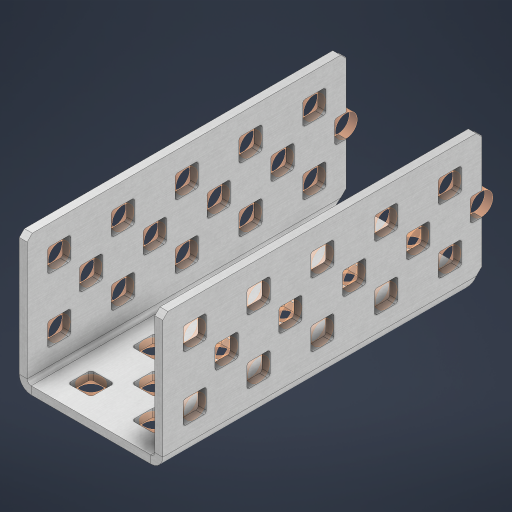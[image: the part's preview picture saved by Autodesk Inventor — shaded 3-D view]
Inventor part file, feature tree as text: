
AUTODESK INVENTOR PART (.ipt)
format: ipt  version: 2023 (Build 270158000, 158)  size: 959,488 bytes
history: native  units: in
note: dims shown in document units (in); Inventor stores cm internally (conversion verified against a paired STEP export)
features: other x66, extrude x58, sheet_metal_op x8, sketch x7, mirror x3, pattern_linear x2, chamfer x1
ambient origin geometry x8: Origin, YZ Plane, XZ Plane, XY Plane, X Axis, Y Axis, Z Axis, Center Point
bodies: Solid1 (feature_tree), Body (feature_tree)
feature tree (145):
  sheet_metal_op  "Flanges"
  sheet_metal_op  "Body Pattern"
  pattern_linear  "Center Pattern"  Spacing1=1.0in  [1 undecoded]
  other  "Arc Length"
  mirror  "Notch Mirror"
  pattern_linear  "Notch Pattern"  Spacing1=0.25in  [1 undecoded]
  other  "Diagonal Plane"
  mirror  "Flange 1"
  mirror  "Flange 2"
  chamfer  "End Chamfer"
  sketch  "Sketch1"  dims[d0=1.0in]
  other  "Plate1"
  sketch  "Sketch2"  dims[d1=2.5in]
  other  "Plate2"
  sheet_metal_op  "Bend1"
  sheet_metal_op  "Corner1"
  sketch  "Sketch8"  dims[d2=0.0625in]
  sketch  "Sketch9"  dims[d3=0.0625in]
  other  "Srf91"
  sheet_metal_op  "Body Pattern Sketch"
  other  "Srf92"
  sketch  "Sketch13"  dims[d4=0.0312in]
  sketch  "Sketch15"  dims[d5=0.125in]
  sketch  "Sketch16"  dims[d6=0.0625in d7=1.0in d8=90.0deg d9=0.0312in d10=0.25in d11=0.0625in d12=0.0625in d49=0.182in d50=0.02in d52=0.25in d53=0.0625in d54=0.0in d55=0.172in d56=1.0in d57=0.0in d60=1.9685in d62=0.5in d63=0.7874in d65=0.5in d85=0.1473in d86=0.1782in d88=0.04in d89=0.0625in d90=0.0in d91=0.04in d92=0.0491in d95=2.5in d96=0.04in d97=0.25in d98=45.0deg d99=0.25in d102=2.497in d106=0.182in d107=0.02in d108=0.5in d110=0.0625in d111=0.0in d112=0.172in d113=0.5in d114=0.0in d117=0.5in d118=0.5in d131=0.25in d132=0.25in]
  other  "Srf786"
  other  "Srf889"
  other  "Srf890"
  other  "Srf891"
  other  "Srf892"
  other  "Srf1315"
  other  "Srf1316"
  other  "Srf1317"
  other  "Srf1325"
  other  "Srf1326"
  other  "Srf1327"
  other  "Srf1328"
  other  "Srf1374"
  other  "Srf1375"
  other  "Srf1376"
  other  "Srf1384"
  other  "Srf1385"
  other  "Srf1386"
  other  "Srf1387"
  other  "Srf1433"
  other  "Srf1434"
  other  "Srf1473"
  other  "Srf1474"
  other  "Srf1475"
  other  "Srf1476"
  other  "Srf1477"
  other  "Srf1500"
  other  "Srf1501"
  other  "Srf1502"
  other  "Srf1503"
  other  "Srf1504"
  other  "Srf1505"
  other  "Srf1506"
  other  "Srf1507"
  other  "Srf1538"
  other  "Srf1539"
  other  "Srf1540"
  other  "Srf1541"
  other  "Srf1542"
  other  "Srf1543"
  other  "Srf1544"
  other  "Srf1545"
  other  "Srf1576"
  other  "Srf1577"
  other  "Srf1578"
  other  "Srf1579"
  other  "Srf1580"
  other  "Srf1581"
  other  "Srf1582"
  other  "Srf1583"
  other  "Srf1614"
  other  "Srf1615"
  other  "Srf1616"
  other  "Srf1617"
  other  "Srf1618"
  other  "Srf1619"
  other  "Srf1620"
  other  "Srf1621"
  sheet_metal_op  "Body Stamp"
  sheet_metal_op  "Body Circle"
  other  "Center Stamp"
  other  "Center Circle"
  sheet_metal_op  "Notch"
  extrude  "ExtrusionSrf92"  Depth=0.0625in
  extrude  "ExtrusionSrf889"  Depth=0.0625in
  extrude  "ExtrusionSrf890"  Depth=0.5in
  extrude  "ExtrusionSrf891"  Depth=0.02in
  extrude  "ExtrusionSrf892"  Depth=0.5in
  extrude  "ExtrusionSrf1315"  Depth=0.0625in
  extrude  "ExtrusionSrf1316"  TaperAngle=0.0deg  [1 undecoded]
  extrude  "ExtrusionSrf1355"  Depth=0.5in
  extrude  "ExtrusionSrf1356"  Depth=1.0in TaperAngle=0.0deg
  extrude  "ExtrusionSrf1357"  Depth=0.5in
  extrude  "ExtrusionSrf1358"  Depth=0.5in
  extrude  "ExtrusionSrf1359"  Depth=0.5in
  extrude  "ExtrusionSrf1374"  Depth=0.5in
  extrude  "ExtrusionSrf1375"  Depth=0.5in
  extrude  "ExtrusionSrf1414"  Depth=0.0625in
  extrude  "ExtrusionSrf1415"  TaperAngle=0.0deg  [1 undecoded]
  extrude  "ExtrusionSrf1416"  Depth=0.5in
  extrude  "ExtrusionSrf1417"  Depth=0.5in
  extrude  "ExtrusionSrf1418"  Depth=2.5in
  extrude  "ExtrusionSrf1433"  Depth=0.5in TaperAngle=45.0deg
  extrude  "ExtrusionSrf1434"  Depth=0.5in
  extrude  "ExtrusionSrf1473"  Depth=0.5in
  extrude  "ExtrusionSrf1474"  Depth=0.5in
  extrude  "ExtrusionSrf1475"  Depth=0.02in
  extrude  "ExtrusionSrf1476"  Depth=0.5in
  extrude  "ExtrusionSrf1477"  Depth=0.0625in
  extrude  "ExtrusionSrf1500"  TaperAngle=0.0deg  [1 undecoded]
  extrude  "ExtrusionSrf1501"  Depth=0.5in
  extrude  "ExtrusionSrf1502"  Depth=0.5in TaperAngle=0.0deg
  extrude  "ExtrusionSrf1503"  Depth=0.5in
  extrude  "ExtrusionSrf1504"  Depth=0.5in
  extrude  "ExtrusionSrf1505"  Depth=0.5in
  extrude  "ExtrusionSrf1506"  Depth=0.5in
  extrude  "ExtrusionSrf1507"  [1 undecoded]
  extrude  "ExtrusionSrf1538"  [1 undecoded]
  extrude  "ExtrusionSrf1539"  [1 undecoded]
  extrude  "ExtrusionSrf1540"  [1 undecoded]
  extrude  "ExtrusionSrf1541"  [1 undecoded]
  extrude  "ExtrusionSrf1542"  [1 undecoded]
  extrude  "ExtrusionSrf1543"  [1 undecoded]
  extrude  "ExtrusionSrf1544"  [1 undecoded]
  extrude  "ExtrusionSrf1545"  [1 undecoded]
  extrude  "ExtrusionSrf1576"  [1 undecoded]
  extrude  "ExtrusionSrf1577"  [1 undecoded]
  extrude  "ExtrusionSrf1578"  [1 undecoded]
  extrude  "ExtrusionSrf1579"  [1 undecoded]
  extrude  "ExtrusionSrf1580"  [1 undecoded]
  extrude  "ExtrusionSrf1581"  [1 undecoded]
  extrude  "ExtrusionSrf1582"  [1 undecoded]
  extrude  "ExtrusionSrf1583"  [1 undecoded]
  extrude  "ExtrusionSrf1614"  [1 undecoded]
  extrude  "ExtrusionSrf1615"  [1 undecoded]
  extrude  "ExtrusionSrf1616"  [1 undecoded]
  extrude  "ExtrusionSrf1617"  [1 undecoded]
  extrude  "ExtrusionSrf1618"  [1 undecoded]
  extrude  "ExtrusionSrf1619"  [1 undecoded]
  extrude  "ExtrusionSrf1620"  [1 undecoded]
  extrude  "ExtrusionSrf1621"  [1 undecoded]
note: 30 required parameter values undecoded (feature->parameter linkage not recoverable at this tier; creation-order binding heuristic only, values carry confidence <= 0.55)
